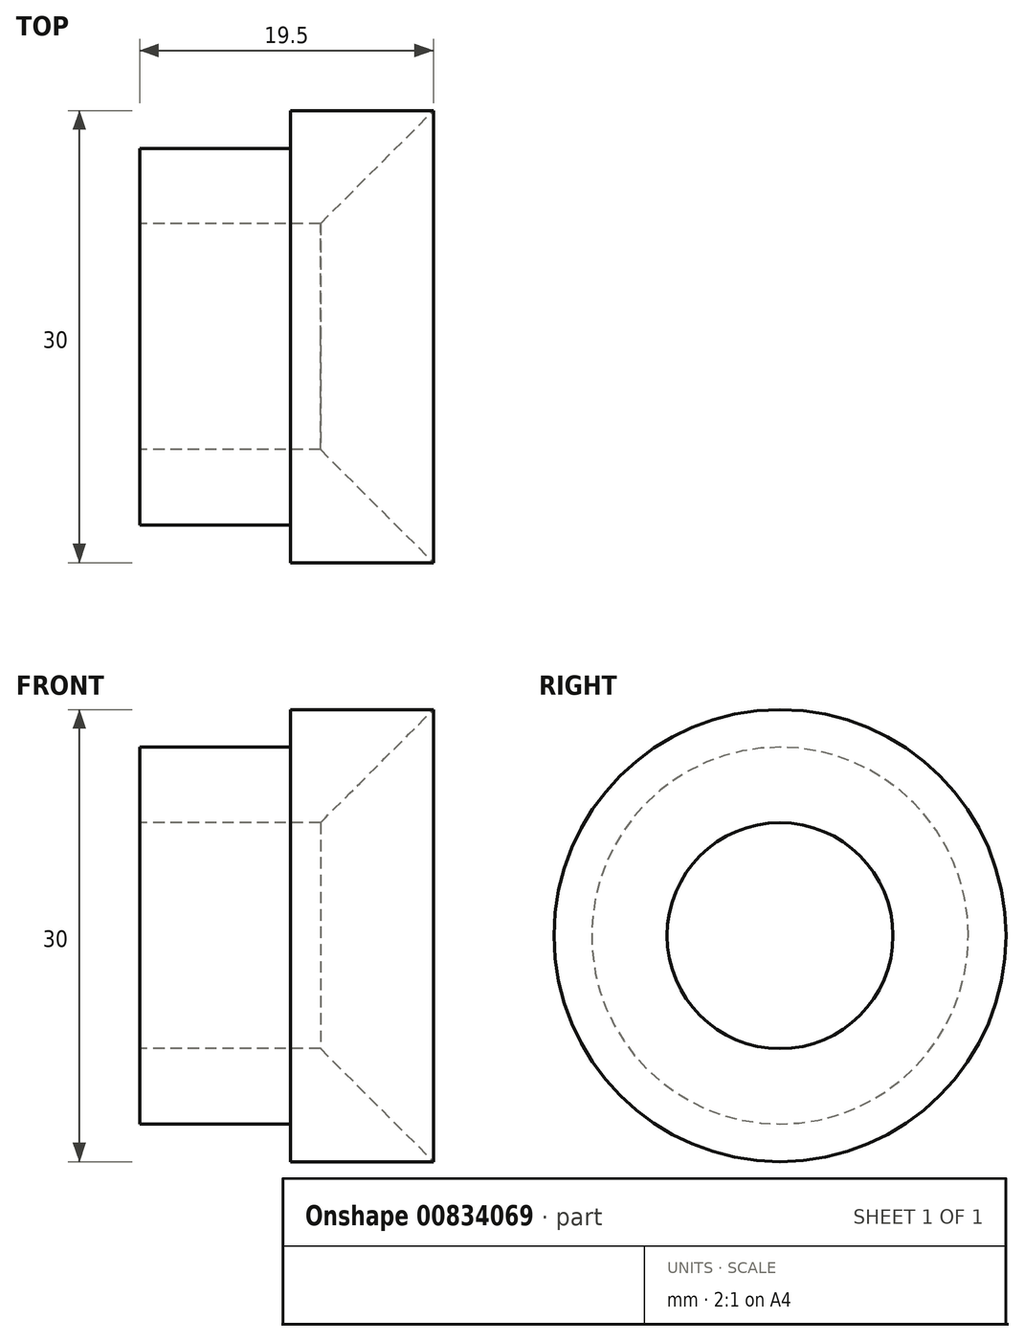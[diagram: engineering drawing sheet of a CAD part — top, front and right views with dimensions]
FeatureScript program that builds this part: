
annotation { "Feature Type Name" : "Feature", "Feature Type Description" : "" }
export const myFeature = defineFeature(function(context is Context, id is Id, definition is map)
    precondition{}
    {
        {
            var Q0;
            Q0=qCreatedBy(makeId("Front.planeOp"),FACE);
            var sketch = newSketch(context, id + "F0", { "sketchPlane" : qUnion([Q0])});
            skLineSegment(sketch, "E0", {"start": v(0, 7.5) * mm, "end": v(12, 7.5) * mm});
            skLineSegment(sketch, "E1", {"start": v(0, 7.5) * mm, "end": v(0, 12.5) * mm});
            skLineSegment(sketch, "E2", {"start": v(0, 12.5) * mm, "end": v(10, 12.5) * mm});
            skLineSegment(sketch, "E3", {"start": v(10, 12.5) * mm, "end": v(10, 15) * mm});
            skLineSegment(sketch, "E4", {"start": v(10, 15) * mm, "end": v(19.5, 15) * mm});
            skLineSegment(sketch, "E5", {"start": v(19.5, 15) * mm, "end": v(12, 7.5) * mm});
            skLineSegment(sketch, "E6", {"start": v(-5.2, 0) * mm, "end": v(24.34, 0) * mm, "construction": true});
            skSolve(sketch);
        }
        {
            var Q0;
            Q0=makeQuery(id+"F0.imprint","IMPRINT",FACE,{"disambiguationData":[TD([[makeQuery(id+"F0.imprint","IMPRINT",EDGE,{"derivedFrom":sQuery(id+"F0.wireOp",EDGE,"E0")}),1.0]])]});
            var Q1;
            Q1=sQuery(id+"F0.wireOp",EDGE,"E6");
            revolve(context, id + "F1", {"surfaceOperationType" : NewSurfaceOperationType.NEW, "entities" : qUnion([Q0]), "axis" : qUnion([Q1]), "revolveType" : RevolveType.FULL});
        }
    });
